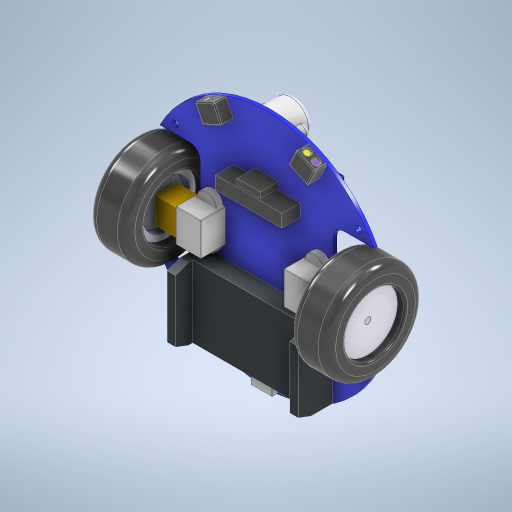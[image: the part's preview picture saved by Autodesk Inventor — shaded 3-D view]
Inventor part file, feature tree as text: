
AUTODESK INVENTOR PART (.ipt)
format: ipt  version: 2023 (Build 270158000, 158)  size: 1,086,976 bytes
history: native  units: mm
features: extrude x23, other x17, sketch x15, fillet x12, projected_geometry x12, mirror x7, plane x2, revolve x1, pattern_linear x1
ambient origin geometry x8: Origin, YZ Plane, XZ Plane, XY Plane, X Axis, Y Axis, Z Axis, Center Point
bodies: Body1 (feature_tree), Body2 (feature_tree), Body3 (feature_tree), Body4 (feature_tree), Body5 (feature_tree), Body6 (feature_tree), Body7 (feature_tree), Body8 (feature_tree), Body9 (feature_tree), Body10 (feature_tree), Body11 (feature_tree), Body12 (feature_tree), Body13 (feature_tree), Body14 (feature_tree), Body15 (feature_tree), Body16 (feature_tree), Body17 (feature_tree), Body18 (feature_tree)
feature tree (90):
  other  "Sólido1"
  extrude  "Extrusión1"  Depth=50.0mm
  fillet  "Empalme1"  Radius=18.5mm
  sketch  "Boceto2"  dims[d3=18.5mm d4=1.6mm d5=0.0mm]
  extrude  "Extrusión2"  Depth=1.6mm TaperAngle=0.0deg
  extrude  "Extrusión3"  Depth=5.0mm
  fillet  "Empalme2"  Radius=5.5mm
  plane  "Plano de trabajo1"
  revolve  "Revolución1"  [1 undecoded]
  mirror  "Simetría1"
  sketch  "Boceto5"  dims[d9=11.5mm d10=0.0mm d11=8.0mm d12=0.0mm]
  extrude  "Extrusión4"  Depth=2.0mm
  extrude  "Extrusión5"  TaperAngle=90.0deg  [1 undecoded]
  pattern_linear  "Patrón rectangular1"  Count1=3 Spacing1=12.5mm
  fillet  "Empalme3"  Radius=30.0mm
  sketch  "Boceto6"  dims[d13=2.0mm d14=9.0mm]
  extrude  "Extrusión6"  Depth=0.25mm
  extrude  "Extrusión7"  Depth=0.25mm
  fillet  "Empalme4"  Radius=2.9mm
  mirror  "Simetría2"
  sketch  "Boceto7"  dims[d15=10.5mm d16=90.0deg]
  extrude  "Extrusión8"  Depth=2.75mm
  fillet  "Empalme5"  Radius=5.1mm
  extrude  "Extrusión9"  Depth=0.25mm TaperAngle=0.0deg
  fillet  "Empalme6"  Radius=0.2mm
  sketch  "Boceto8"  dims[d17=5.0mm]
  extrude  "Extrusión10"  Depth=4.0mm
  extrude  "Extrusión11"  Depth=5.0mm
  sketch  "Boceto9"  dims[d18=6.6mm]
  extrude  "Extrusión12"  Depth=0.25mm
  mirror  "Simetría3"
  mirror  "Simetría4"
  extrude  "Extrusión13"  Depth=0.25mm
  fillet  "Empalme7"  Radius=3.0mm
  extrude  "Extrusión14"  Depth=0.25mm
  fillet  "Empalme8"  Radius=5.0mm
  mirror  "Simetría6"
  extrude  "Extrusión15"  Depth=0.25mm
  extrude  "Extrusión16"  Depth=0.25mm
  sketch  "Boceto14"  dims[d23=6.55mm d24=0.0mm]
  extrude  "Extrusión17"  Depth=0.25mm
  extrude  "Extrusión18"  Depth=3.0mm
  extrude  "Extrusión19"  Depth=0.25mm
  fillet  "Empalme9"  Radius=2.6mm
  fillet  "Empalme10"  Radius=1.2mm
  fillet  "Empalme11"  Radius=16.0mm
  mirror  "Simetría7"
  sketch  "Boceto15"  dims[d25=6.25mm d26=0.0mm d27=30.0mm d29=12.5mm d30=30.0mm d32=12.5mm]
  extrude  "Extrusión20"  Depth=1.25mm TaperAngle=0.0deg
  extrude  "Extrusión21"  Depth=0.2mm
  mirror  "Simetría8"
  extrude  "Extrusión22"  Depth=1.5mm TaperAngle=0.0deg
  extrude  "Extrusión23"  Depth=0.2mm
  fillet  "Empalme12"  Radius=11.5mm
  sketch  "Boceto1"  dims[d0=110.0mm d1=50.0mm d2=18.5mm]
  other  "Sólido2"
  other  "Sólido3"
  sketch  "Boceto4"  dims[d6=5.0mm d7=15.75mm d8=5.5mm]
  projected_geometry  "Contorno proyectado1"
  other  "Sólido4"
  projected_geometry  "Contorno proyectado2"
  other  "IR_S1"
  projected_geometry  "Contorno proyectado3"
  other  "Sólido6"
  projected_geometry  "Contorno proyectado4"
  other  "Sólido7"
  other  "Sólido8"
  projected_geometry  "Contorno proyectado5"
  other  "Sólido9"
  other  "Sólido10"
  projected_geometry  "Contorno proyectado6"
  sketch  "Boceto10"  dims[d19=2.25mm]
  projected_geometry  "Contorno proyectado7"
  sketch  "Boceto11"  dims[d20=1.65mm]
  sketch  "Boceto12"  dims[d21=1.65mm]
  projected_geometry  "Contorno proyectado8"
  other  "Sólido12"
  sketch  "Boceto13"  dims[d22=32.5mm]
  projected_geometry  "Contorno proyectado9"
  other  "Sólido13"
  projected_geometry  "Contorno proyectado10"
  other  "Sólido14"
  other  "Sólido15"
  projected_geometry  "Contorno proyectado11"
  other  "Sólido16"
  sketch  "Boceto16"  dims[d33=0.2mm d34=6.9mm d35=4.5mm d36=2.9mm d37=2.75mm d38=5.1mm d39=0.0mm d40=4.9mm d41=0.0mm d42=0.2mm d43=4.0mm d44=5.0mm d45=3.15mm d46=12.5mm d47=3.0mm d48=12.5mm d49=5.0mm d50=7.15mm d51=6.5mm d52=11.25mm d53=3.0mm d54=6.0mm d55=2.6mm d56=1.2mm d57=16.0mm d58=1.25mm d59=0.0mm d60=0.2mm d61=1.5mm d62=0.0mm d63=0.2mm d64=11.5mm d65=15.25mm d66=9.25mm d67=15.0mm d68=11.25mm d69=0.0mm d70=3.0mm d71=0.0mm d72=12.0mm d73=9.95mm d74=3.0mm d75=26.04mm d76=41.91mm d77=10.0mm d78=0.0mm d79=4.363323mm d80=9.55mm d81=8.25mm d82=5.5mm d83=0.0mm d84=0.5mm d85=3.0mm d86=2.25mm d87=2.25mm d88=0.5mm d89=0.0mm d90=0.25mm d91=10.75mm d92=0.0mm d93=2.9mm d94=10.0mm d95=0.0mm d96=8.5mm d97=27.5mm d98=21.5mm d99=10.0mm d100=0.0mm d101=7.0mm d102=0.0mm d103=3.5mm d104=14.0mm d105=0.0mm d106=0.0mm d107=4.0mm d108=1.0mm d109=0.25mm d110=5.85mm d111=30.5mm d112=32.85mm d113=60.0mm d114=7.85mm d115=0.0mm d116=28.35mm d117=7.84mm d118=2.0mm d119=3.85mm d120=0.0mm d121=33.6mm d122=10.75mm d123=2.6mm d124=1.0mm d125=8.35mm d126=0.0mm d127=9.753451mm d128=5.25mm d130=2.5mm d131=0.0mm d132=0.25mm]
  projected_geometry  "Contorno proyectado12"
  plane  "Plano de trabajo2"
  other  "Sólido17"
  other  "Sólido18"
note: 2 required parameter values undecoded (feature->parameter linkage not recoverable at this tier; creation-order binding heuristic only, values carry confidence <= 0.55)